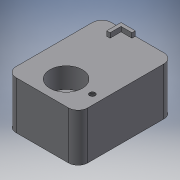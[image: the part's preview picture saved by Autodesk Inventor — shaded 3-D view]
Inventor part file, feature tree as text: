
AUTODESK INVENTOR PART (.ipt)
format: ipt  version: 2019 (Build 230136000, 136)  size: 146,944 bytes
history: native  units: mm
features: sketch x5, extrude x3, hole x2, fillet x1
ambient origin geometry x8: Origin, YZ Plane, XZ Plane, XY Plane, X Axis, Y Axis, Z Axis, Center Point
bodies: Solid1 (feature_tree)
feature tree (11):
  extrude  "Extrusion1"  Depth=20.0mm
  extrude  "Extrusion2"  Depth=3.0mm
  fillet  "Fillet1"  Radius=0.7mm
  hole  "Hole2"  [1 undecoded]
  hole  "Hole4"  [1 undecoded]
  extrude  "Extrusion3"  Depth=2.0mm
  sketch  "Sketch1"  dims[d0=15.0mm d1=20.0mm]
  sketch  "Sketch2"  dims[d2=10.0mm d3=0.0mm d4=3.0mm d5=0.7mm]
  sketch  "Sketch4"  dims[d7=4.0mm d8=1.0mm d9=0.0mm]
  sketch  "Sketch6"  dims[d10=2.0mm d19=2.0mm]
  sketch  "Sketch7"  dims[d21=1.181mm d22=3.048mm d23=4.369mm d24=2.0mm d25=14.3117mm d26=4.636mm d27=20.594885mm d29=6.0mm d38=5.0mm d39=4.496mm d40=8.331mm d41=8.433mm d42=2.0mm d43=14.3117mm d44=12.3mm d45=20.594885mm d46=6.8mm d47=4.3mm d48=0.0mm d49=2.0mm]
note: 2 required parameter values undecoded (feature->parameter linkage not recoverable at this tier; creation-order binding heuristic only, values carry confidence <= 0.55)
